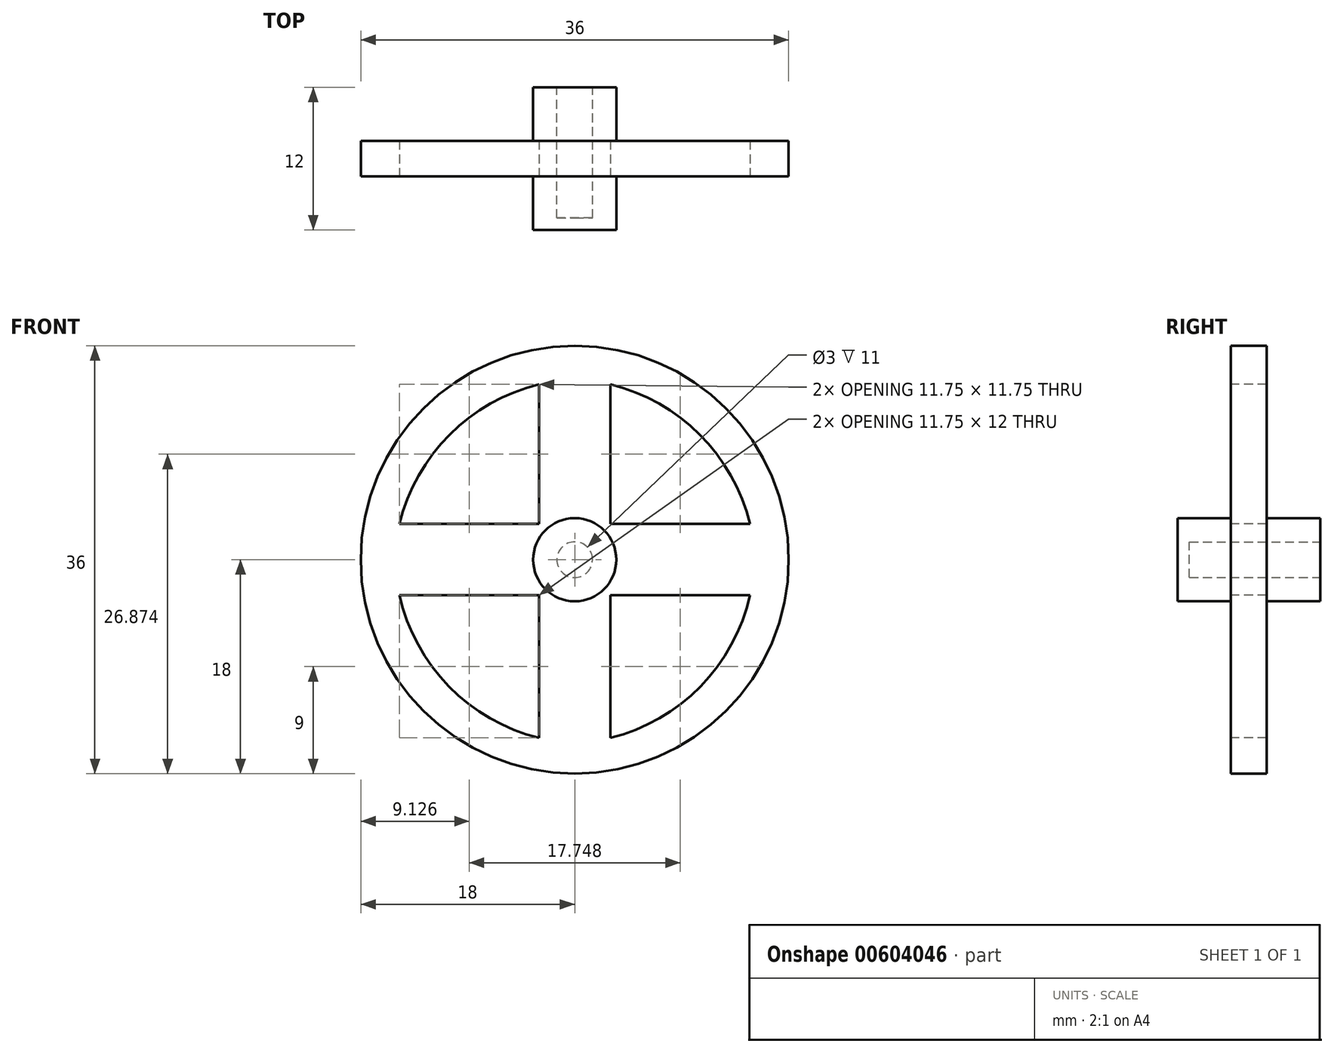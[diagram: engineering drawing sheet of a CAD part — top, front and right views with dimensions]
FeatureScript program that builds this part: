
annotation { "Feature Type Name" : "Feature", "Feature Type Description" : "" }
export const myFeature = defineFeature(function(context is Context, id is Id, definition is map)
    precondition{}
    {
        {
            var Q0;
            Q0=qCreatedBy(makeId("Front.planeOp"),FACE);
            var sketch = newSketch(context, id + "F0", { "sketchPlane" : qUnion([Q0])});
            skCircle(sketch, "E0", {"center": v(0, 0) * mm, "radius": 18 * mm});
            skCircle(sketch, "E1", {"center": v(0, 0) * mm, "radius": 3.5 * mm});
            skCircle(sketch, "E2", {"center": v(0, 0) * mm, "radius": 1.5 * mm});
            skSolve(sketch);
        }
        {
            var Q0;
            Q0=makeQuery(id+"F0.imprint","IMPRINT",FACE,{"disambiguationData":[TD([[makeQuery(id+"F0.imprint","IMPRINT",EDGE,{"derivedFrom":sQuery(id+"F0.wireOp",EDGE,"E0")}),1.0]])]});
            extrude(context, id + "F1", {"entities" : qUnion([Q0]), "depth" : 3 * mm});
        }
        {
            var Q0;
            Q0=makeQuery(id+"F0.imprint","IMPRINT",FACE,{"disambiguationData":[TD([[makeQuery(id+"F0.imprint","IMPRINT",EDGE,{"derivedFrom":sQuery(id+"F0.wireOp",EDGE,"E1")}),1.0]])]});
            extrude(context, id + "F2", {"entities" : qUnion([Q0]), "operationType" : NewBodyOperationType.ADD, "depth" : 7.5 * mm});
        }
        {
            var Q0;
            Q0=makeQuery(id+"F2.opExtrude","CAP_FACE",FACE,{"disambiguationData":[OSD([sQuery(id+"F0.wireOp",EDGE,"E1"),sQuery(id+"F0.wireOp",EDGE,"E2")])],"isStart":false});
            extrude(context, id + "F3", {"entities" : qUnion([Q0]), "operationType" : NewBodyOperationType.ADD, "oppositeDirection" : true, "depth" : 12 * mm});
        }
        {
            var Q0;
            Q0=makeQuery(id+"F1.opExtrude","CAP_FACE",FACE,{"disambiguationData":[OSD([sQuery(id+"F0.wireOp",EDGE,"E0"),sQuery(id+"F0.wireOp",EDGE,"E1")])],"isStart":false});
            var sketch = newSketch(context, id + "F4", { "sketchPlane" : qUnion([Q0])});
            skLineSegment(sketch, "E3", {"start": v(0, 18) * mm, "end": v(0, -18) * mm});
            skLineSegment(sketch, "E4", {"start": v(18, 0) * mm, "end": v(-18, 0) * mm});
            skLineSegment(sketch, "E5", {"start": v(0, -6.35) * mm, "end": v(-3, -6.35) * mm, "construction": true});
            skLineSegment(sketch, "E6", {"start": v(-3, -18) * mm, "end": v(-3, -15) * mm, "construction": true});
            skLineSegment(sketch, "E7", {"start": v(-3, -1.8) * mm, "end": v(-3, -15) * mm});
            skLineSegment(sketch, "E8", {"start": v(-7, 0) * mm, "end": v(-7, -3) * mm, "construction": true});
            skLineSegment(sketch, "E9", {"start": v(-17.75, -3) * mm, "end": v(-14.75, -3) * mm, "construction": true});
            skLineSegment(sketch, "E10", {"start": v(-14.75, -3) * mm, "end": v(-1.8, -3) * mm});
            skArc(sketch, "E11", {"start": v(-14.75, -3) * mm, "mid": v(-10.58, -10.67) * mm, "end": v(-3, -15) * mm});
            skLineSegment(sketch, "E12", {"start": v(-3, 17.75) * mm, "end": v(-3, 14.75) * mm, "construction": true});
            skLineSegment(sketch, "E13", {"start": v(0, 5.67) * mm, "end": v(-3, 5.67) * mm, "construction": true});
            skLineSegment(sketch, "E14", {"start": v(-10.49, 0) * mm, "end": v(-10.49, 3) * mm, "construction": true});
            skLineSegment(sketch, "E15", {"start": v(0, -7.24) * mm, "end": v(3, -7.24) * mm, "construction": true});
            skLineSegment(sketch, "E16", {"start": v(-3, -15) * mm, "end": v(-3, -3) * mm});
            skLineSegment(sketch, "E17", {"start": v(3, -3) * mm, "end": v(3, -15) * mm});
            skLineSegment(sketch, "E18", {"start": v(17.75, -3) * mm, "end": v(14.75, -3) * mm, "construction": true});
            skLineSegment(sketch, "E19", {"start": v(3, -3) * mm, "end": v(14.75, -3) * mm});
            skArc(sketch, "E20", {"start": v(3, -15) * mm, "mid": v(10.58, -10.67) * mm, "end": v(14.75, -3) * mm});
            skLineSegment(sketch, "E21", {"start": v(-3, 3) * mm, "end": v(-3, 14.75) * mm});
            skLineSegment(sketch, "E22", {"start": v(-3, 3) * mm, "end": v(-14.75, 3) * mm});
            skArc(sketch, "E23", {"start": v(-3, 14.75) * mm, "mid": v(-10.52, 10.52) * mm, "end": v(-14.75, 3) * mm});
            skLineSegment(sketch, "E24", {"start": v(3, 3) * mm, "end": v(14.75, 3) * mm});
            skLineSegment(sketch, "E25", {"start": v(3, 3) * mm, "end": v(3, 14.75) * mm});
            skArc(sketch, "E26", {"start": v(14.75, 3) * mm, "mid": v(10.52, 10.52) * mm, "end": v(3, 14.75) * mm});
            skSolve(sketch);
        }
        {
            var Q0;
            Q0=makeQuery(id+"F4.imprint","IMPRINT",FACE,{"disambiguationData":[TD([[makeQuery(id+"F4.imprint","IMPRINT",EDGE,{"derivedFrom":sQuery(id+"F4.wireOp",EDGE,"E21")}),1.0]])]});
            var Q1;
            Q1=makeQuery(id+"F4.imprint","IMPRINT",FACE,{"disambiguationData":[TD([[makeQuery(id+"F4.imprint","IMPRINT",EDGE,{"derivedFrom":sQuery(id+"F4.wireOp",EDGE,"E24")}),1.0]])]});
            var Q2;
            {var subQ2=sQuery(id+"F4.wireOp",EDGE,"E11");Q2=makeQuery(id+"F4.imprint","IMPRINT",FACE,{"disambiguationData":[TD([[makeQuery(id+"F4.imprint","IMPRINT",EDGE,{"derivedFrom":subQ2}),1.0]])]});}
            var Q3;
            Q3=makeQuery(id+"F4.imprint","IMPRINT",FACE,{"disambiguationData":[TD([[makeQuery(id+"F4.imprint","IMPRINT",EDGE,{"derivedFrom":sQuery(id+"F4.wireOp",EDGE,"E17")}),1.0]])]});
            extrude(context, id + "F5", {"entities" : qUnion([Q0, Q1, Q2, Q3]), "operationType" : NewBodyOperationType.REMOVE, "oppositeDirection" : true, "depth" : 250 * mm});
        }
        {
            var Q0;
            Q0=makeQuery(id+"F2.opExtrude","CAP_FACE",FACE,{"disambiguationData":[OSD([sQuery(id+"F0.wireOp",EDGE,"E1"),sQuery(id+"F0.wireOp",EDGE,"E2")])],"isStart":false});
            var sketch = newSketch(context, id + "F6", { "sketchPlane" : qUnion([Q0])});
            skCircle(sketch, "E27", {"center": v(0, 0) * mm, "radius": 2.52 * mm});
            skSolve(sketch);
        }
        {
            var Q0;
            Q0=qSketchRegion(id+"F6",true);
            extrude(context, id + "F7", {"entities" : qUnion([Q0]), "operationType" : NewBodyOperationType.ADD, "oppositeDirection" : true, "depth" : 1 * mm});
        }
    });
